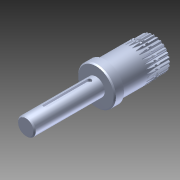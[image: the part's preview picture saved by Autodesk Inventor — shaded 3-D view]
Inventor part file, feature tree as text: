
AUTODESK INVENTOR PART (.ipt)
format: ipt  version: 2014 SP1 (Build 180222100, 222)  size: 2,121,216 bytes
history: native  units: in
note: dims shown in document units (in); Inventor stores cm internally (conversion verified against a paired STEP export)
features: imported_body x2, other x1, chamfer x1
ambient origin geometry x8: Origin, YZ Plane, XZ Plane, XY Plane, X Axis, Y Axis, Z Axis, Center Point
bodies: Body1 (feature_tree), Body2 (feature_tree)
feature tree (4):
  other  "8MM CIM SHAFT"
  chamfer  "Chamfer3"  [1 undecoded]
  imported_body  "Base1"
  imported_body  "Base2"
note: 1 required parameter value undecoded (feature->parameter linkage not recoverable at this tier; creation-order binding heuristic only, values carry confidence <= 0.55)
